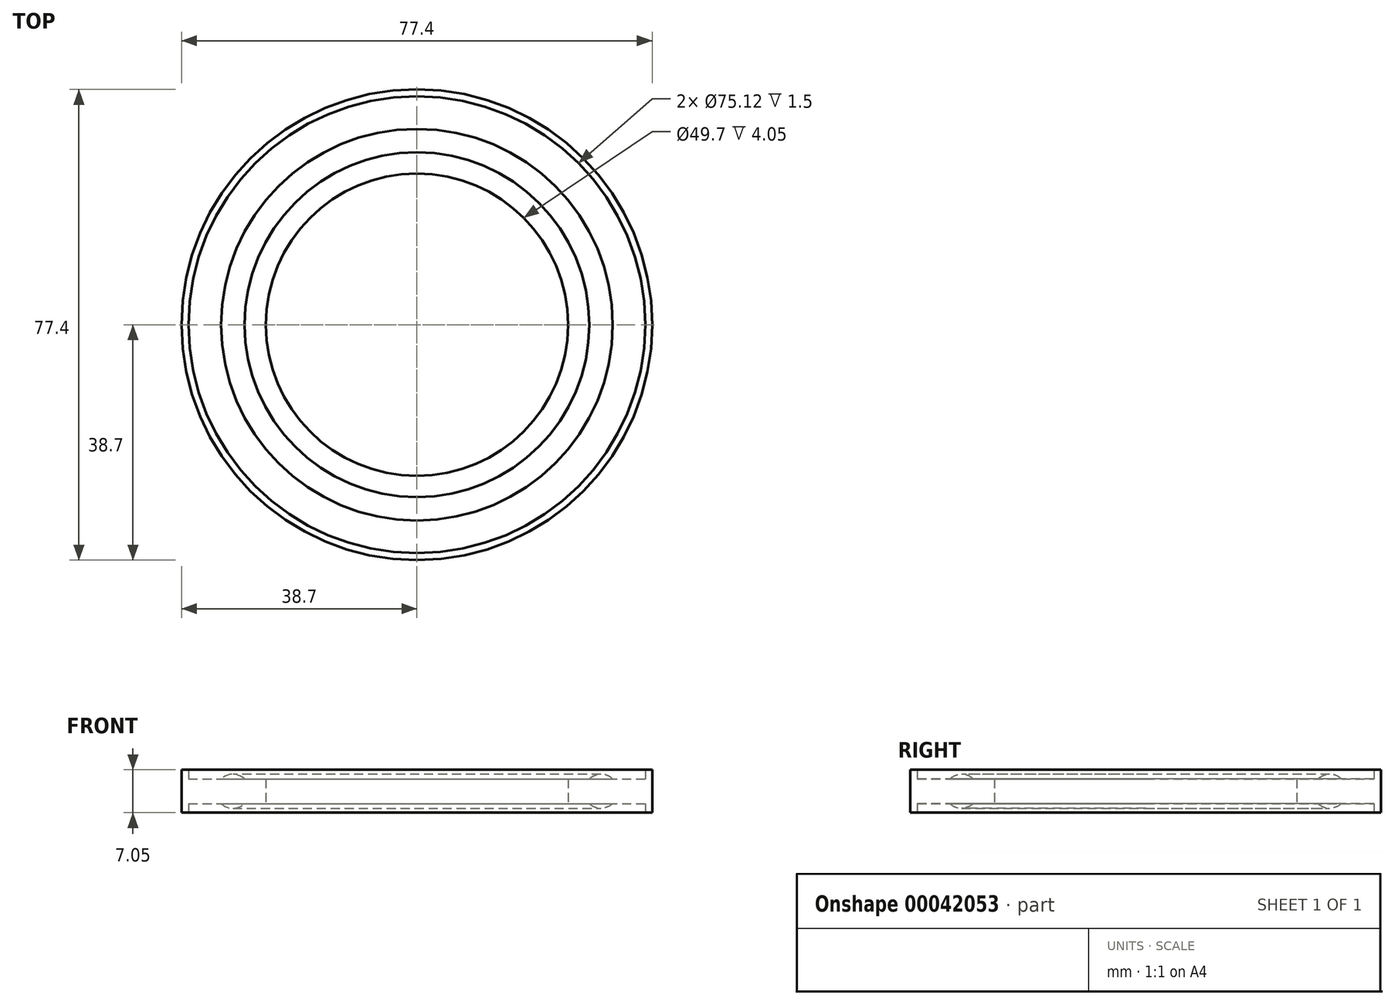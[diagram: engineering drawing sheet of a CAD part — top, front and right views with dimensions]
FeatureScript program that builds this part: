
annotation { "Feature Type Name" : "Feature", "Feature Type Description" : "" }
export const myFeature = defineFeature(function(context is Context, id is Id, definition is map)
    precondition{}
    {
        {
            var Q0;
            Q0=qCreatedBy(makeId("Front.planeOp"),FACE);
            var sketch = newSketch(context, id + "F0", { "sketchPlane" : qUnion([Q0])});
            skLineSegment(sketch, "E0", {"start": v(0, 0) * mm, "end": v(0, 7.05) * mm, "construction": true});
            skLineSegment(sketch, "E1", {"start": v(38.7, 0) * mm, "end": v(38.7, 7.05) * mm});
            skLineSegment(sketch, "E2", {"start": v(38.7, 7.05) * mm, "end": v(37.56, 7.05) * mm});
            skLineSegment(sketch, "E3", {"start": v(37.56, 7.05) * mm, "end": v(37.56, 5.55) * mm});
            skLineSegment(sketch, "E4", {"start": v(37.56, 5.55) * mm, "end": v(32.2, 5.55) * mm});
            skLineSegment(sketch, "E5", {"start": v(38.7, 0) * mm, "end": v(37.56, 0) * mm});
            skLineSegment(sketch, "E6", {"start": v(37.56, 0) * mm, "end": v(37.56, 1.5) * mm});
            skLineSegment(sketch, "E7", {"start": v(37.56, 1.5) * mm, "end": v(32.2, 1.5) * mm});
            skLineSegment(sketch, "E8", {"start": v(32.2, 1.5) * mm, "end": v(24.85, 1.5) * mm, "construction": true});
            skLineSegment(sketch, "E9", {"start": v(24.85, 1.5) * mm, "end": v(24.85, 5.55) * mm});
            skLineSegment(sketch, "E10", {"start": v(24.85, 5.55) * mm, "end": v(28.35, 5.55) * mm});
            skLineSegment(sketch, "E11", {"start": v(24.85, 1.5) * mm, "end": v(28.35, 1.5) * mm});
            skLineSegment(sketch, "E12", {"start": v(28.35, 1.5) * mm, "end": v(32.2, 5.55) * mm, "construction": true});
            skCircle(sketch, "E13", {"center": v(30.28, 3.52) * mm, "radius": 2.8 * mm});
            skSolve(sketch);
        }
        {
            var Q0;
            Q0=makeQuery(id+"F0.imprint","IMPRINT",FACE,{"disambiguationData":[TD([[makeQuery(id+"F0.imprint","IMPRINT",EDGE,{"derivedFrom":sQuery(id+"F0.wireOp",EDGE,"E9")}),-1.0]])]});
            var Q1;
            Q1=makeQuery(id+"F0.imprint","IMPRINT",FACE,{"disambiguationData":[TD([[makeQuery(id+"F0.imprint","IMPRINT",EDGE,{"derivedFrom":sQuery(id+"F0.wireOp",EDGE,"E1")}),1.0]])]});
            var Q2;
            {var subQ0=sQuery(id+"F0.wireOp",EDGE,"E13");var subQ2=makeQuery(id+"F0.imprint","INTERSECT",VERTEX,{"derivedFrom":[sQuery(id+"F0.wireOp",EDGE,"E4"),subQ0]});Q2=makeQuery(id+"F0.imprint","IMPRINT",FACE,{"disambiguationData":[TD([[makeQuery(id+"F0.imprint","IMPRINT",EDGE,{"disambiguationData":[TD([[subQ2,-1.0]])],"derivedFrom":subQ0}),1.0]])]});}
            var Q3;
            Q3=sQuery(id+"F0.wireOp",EDGE,"E0");
            revolve(context, id + "F1", {"entities" : qUnion([Q0, Q1, Q2]), "axis" : qUnion([Q3]), "revolveType" : RevolveType.FULL});
        }
    });
